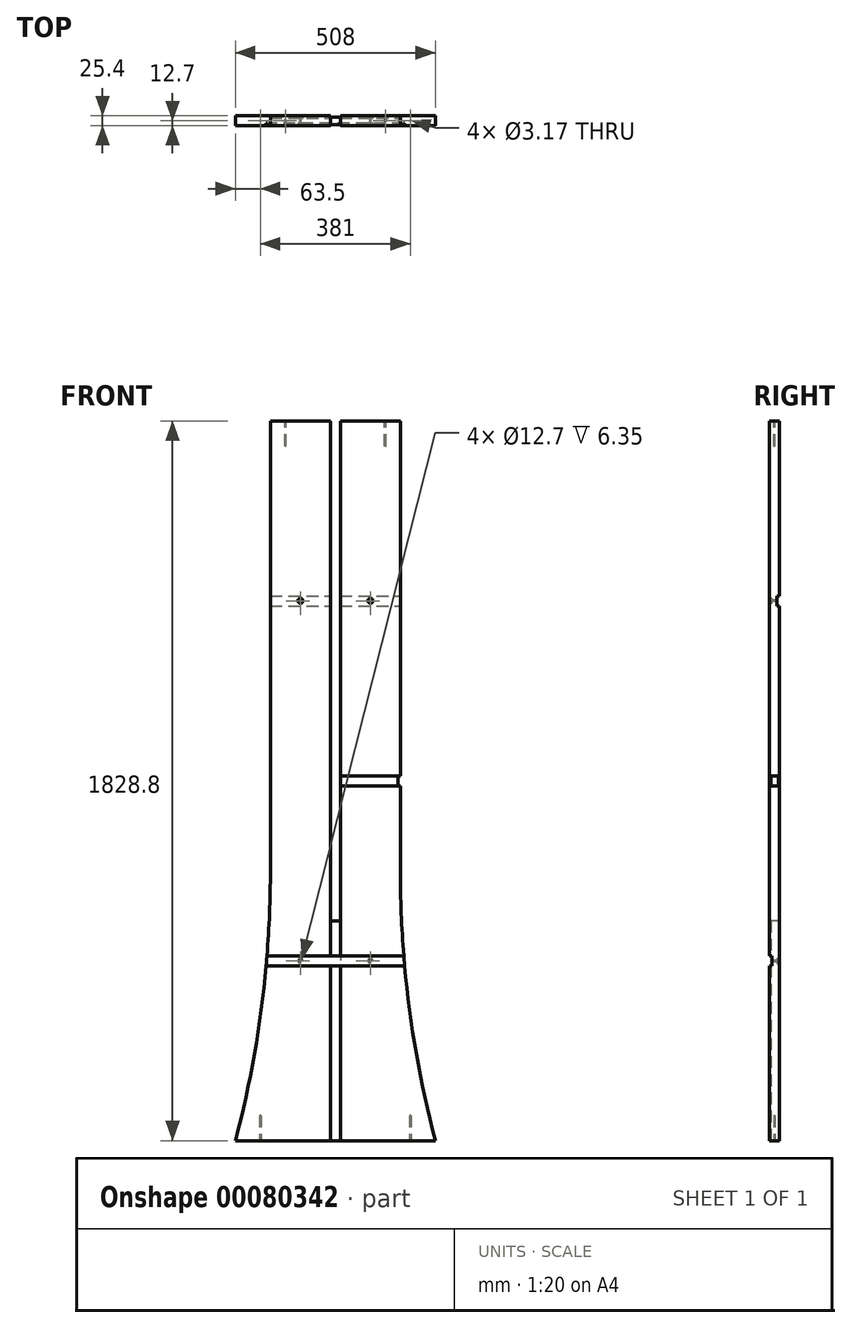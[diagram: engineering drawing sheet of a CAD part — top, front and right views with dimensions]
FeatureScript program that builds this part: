
annotation { "Feature Type Name" : "Feature", "Feature Type Description" : "" }
export const myFeature = defineFeature(function(context is Context, id is Id, definition is map)
    precondition{}
    {
        {
            var Q0;
            Q0=qCreatedBy(makeId("Front.planeOp"),FACE);
            var sketch = newSketch(context, id + "F0", { "sketchPlane" : qUnion([Q0])});
            skLineSegment(sketch, "E0", {"start": v(0, 0) * mm, "end": v(0, 1828.8) * mm, "construction": true});
            skLineSegment(sketch, "E1", {"start": v(0, 1828.8) * mm, "end": v(-165.1, 1828.8) * mm});
            skLineSegment(sketch, "E2", {"start": v(0, 0) * mm, "end": v(-254, 0) * mm});
            skLineSegment(sketch, "E3", {"start": v(-165.1, 1828.8) * mm, "end": v(-165.1, 685.8) * mm});
            skArc(sketch, "E4", {"start": v(-254, 0) * mm, "mid": v(-187.42, 340.03) * mm, "end": v(-165.1, 685.8) * mm});
            skLineSegment(sketch, "E5.MirrorCS", {"start": v(0, 1828.8) * mm, "end": v(165.1, 1828.8) * mm});
            skLineSegment(sketch, "E6.MirrorCS", {"start": v(165.1, 1828.8) * mm, "end": v(165.1, 685.8) * mm});
            skArc(sketch, "E7.MirrorCS", {"start": v(254, 0) * mm, "mid": v(187.42, 340.03) * mm, "end": v(165.1, 685.8) * mm});
            skLineSegment(sketch, "E8.MirrorCS", {"start": v(0, 0) * mm, "end": v(254, 0) * mm});
            skSolve(sketch);
        }
        {
            var Q0;
            Q0=makeQuery(id+"F0.imprint","IMPRINT",FACE,{"disambiguationData":[TD([[makeQuery(id+"F0.imprint","IMPRINT",EDGE,{"derivedFrom":sQuery(id+"F0.wireOp",EDGE,"E1")}),1.0]])]});
            extrude(context, id + "F1", {"entities" : qUnion([Q0]), "endBound" : BoundingType.SYMMETRIC, "depth" : 25.4 * mm});
        }
        {
            var Q0;
            Q0=makeQuery(id+"F1.opExtrude","CAP_FACE",FACE,{"disambiguationData":[OSD([sQuery(id+"F0.wireOp",EDGE,"E1"),sQuery(id+"F0.wireOp",EDGE,"E2"),sQuery(id+"F0.wireOp",EDGE,"E3"),sQuery(id+"F0.wireOp",EDGE,"E4"),sQuery(id+"F0.wireOp",EDGE,"E6.MirrorCS"),sQuery(id+"F0.wireOp",EDGE,"E5.MirrorCS"),sQuery(id+"F0.wireOp",EDGE,"E7.MirrorCS"),sQuery(id+"F0.wireOp",EDGE,"E8.MirrorCS")])],"isStart":false});
            var sketch = newSketch(context, id + "F24", { "sketchPlane" : qUnion([Q0])});
            skLineSegment(sketch, "E9", {"start": v(0, 1828.8) * mm, "end": v(0, 1828.8) * mm});
            skLineSegment(sketch, "E10", {"start": v(0, 1828.8) * mm, "end": v(0, 558.8) * mm, "construction": true});
            skLineSegment(sketch, "E11", {"start": v(0, 558.8) * mm, "end": v(12.7, 558.8) * mm});
            skLineSegment(sketch, "E12", {"start": v(12.7, 1828.8) * mm, "end": v(12.7, 558.8) * mm});
            skLineSegment(sketch, "E13", {"start": v(12.7, 1828.8) * mm, "end": v(0, 1828.8) * mm});
            skLineSegment(sketch, "E14.MirrorCS", {"start": v(-12.7, 1828.8) * mm, "end": v(-12.7, 558.8) * mm});
            skLineSegment(sketch, "E15.MirrorCS", {"start": v(0, 558.8) * mm, "end": v(-12.7, 558.8) * mm});
            skLineSegment(sketch, "E16.MirrorCS", {"start": v(-12.7, 1828.8) * mm, "end": v(0, 1828.8) * mm});
            skSolve(sketch);
        }
        {
            var Q0;
            Q0 = qSketchRegion(id + "F24", true);
            extrude(context, id + "F25", {"entities" : qUnion([Q0]), "operationType" : NewBodyOperationType.REMOVE, "oppositeDirection" : true, "depth" : 38.1 * mm});
        }
        {
            var Q0;
            Q0=makeQuery(id+"F1.opExtrude","CAP_FACE",FACE,{"disambiguationData":[OSD([sQuery(id+"F0.wireOp",EDGE,"E1"),sQuery(id+"F0.wireOp",EDGE,"E2"),sQuery(id+"F0.wireOp",EDGE,"E3"),sQuery(id+"F0.wireOp",EDGE,"E4"),sQuery(id+"F0.wireOp",EDGE,"E6.MirrorCS"),sQuery(id+"F0.wireOp",EDGE,"E5.MirrorCS"),sQuery(id+"F0.wireOp",EDGE,"E7.MirrorCS"),sQuery(id+"F0.wireOp",EDGE,"E8.MirrorCS")])],"isStart":false});
            var sketch = newSketch(context, id + "F2", { "sketchPlane" : qUnion([Q0])});
            skPoint(sketch, "E17", {"position": v(-88.9, 1371.6) * mm});
            skPoint(sketch, "E18", {"position": v(88.9, 1371.6) * mm});
            skSolve(sketch);
        }
        {
            var Q0;
            Q0=sQuery(id+"F2.wireOp",VERTEX,"E17");
            var Q1;
            Q1=sQuery(id+"F2.wireOp",VERTEX,"E18");
            var Q2;
            Q2=makeQuery(id+"F1.opExtrude","SWEPT_BODY",BODY,{"disambiguationData":[OSD([sQuery(id+"F0.wireOp",EDGE,"E1"),sQuery(id+"F0.wireOp",EDGE,"E2"),sQuery(id+"F0.wireOp",EDGE,"E3"),sQuery(id+"F0.wireOp",EDGE,"E4"),sQuery(id+"F0.wireOp",EDGE,"E6.MirrorCS"),sQuery(id+"F0.wireOp",EDGE,"E5.MirrorCS"),sQuery(id+"F0.wireOp",EDGE,"E7.MirrorCS"),sQuery(id+"F0.wireOp",EDGE,"E8.MirrorCS")])]});
            hole(context, id + "F3", {"style" : HoleStyle.C_BORE, "endStyle" : HoleEndStyle.BLIND, "holeDiameter" : 3.17 * mm, "cBoreDiameter" : 12.7 * mm, "cBoreDepth" : 6.35 * mm, "holeDepth" : 63.5 * mm, "locations" : qUnion([Q0, Q1]), "scope" : qUnion([Q2])});
        }
        {
            var Q0;
            Q0=makeQuery(id+"F1.opExtrude","CAP_FACE",FACE,{"disambiguationData":[OSD([sQuery(id+"F0.wireOp",EDGE,"E1"),sQuery(id+"F0.wireOp",EDGE,"E2"),sQuery(id+"F0.wireOp",EDGE,"E3"),sQuery(id+"F0.wireOp",EDGE,"E4"),sQuery(id+"F0.wireOp",EDGE,"E6.MirrorCS"),sQuery(id+"F0.wireOp",EDGE,"E5.MirrorCS"),sQuery(id+"F0.wireOp",EDGE,"E7.MirrorCS"),sQuery(id+"F0.wireOp",EDGE,"E8.MirrorCS")])],"isStart":true});
            var sketch = newSketch(context, id + "F4", { "sketchPlane" : qUnion([Q0])});
            skPoint(sketch, "E19", {"position": v(-88.9, 457.2) * mm});
            skPoint(sketch, "E20", {"position": v(88.9, 457.2) * mm});
            skSolve(sketch);
        }
        {
            var Q0;
            Q0=sQuery(id+"F4.wireOp",VERTEX,"E19");
            var Q1;
            Q1=sQuery(id+"F4.wireOp",VERTEX,"E20");
            var Q2;
            Q2=makeQuery(id+"F1.opExtrude","SWEPT_BODY",BODY,{"disambiguationData":[OSD([sQuery(id+"F0.wireOp",EDGE,"E1"),sQuery(id+"F0.wireOp",EDGE,"E2"),sQuery(id+"F0.wireOp",EDGE,"E3"),sQuery(id+"F0.wireOp",EDGE,"E4"),sQuery(id+"F0.wireOp",EDGE,"E6.MirrorCS"),sQuery(id+"F0.wireOp",EDGE,"E5.MirrorCS"),sQuery(id+"F0.wireOp",EDGE,"E7.MirrorCS"),sQuery(id+"F0.wireOp",EDGE,"E8.MirrorCS")])]});
            hole(context, id + "F5", {"style" : HoleStyle.C_BORE, "endStyle" : HoleEndStyle.BLIND, "holeDiameter" : 3.17 * mm, "cBoreDiameter" : 12.7 * mm, "cBoreDepth" : 6.35 * mm, "holeDepth" : 63.5 * mm, "locations" : qUnion([Q0, Q1]), "scope" : qUnion([Q2])});
        }
        {
            var Q0;
            {var subQ2=sQuery(id+"F0.wireOp",EDGE,"E5.MirrorCS");var subQ5=sQuery(id+"F0.wireOp",EDGE,"E3");var subQ7=sQuery(id+"F0.wireOp",EDGE,"E1");Q0=makeQuery(id+"F25.boolean.opBoolean","SPLIT",FACE,{"disambiguationData":[TD([makeQuery(id+"F1.opExtrude","SWEPT_FACE",FACE,{"disambiguationData":[OSD([subQ5])]})])],"derivedFrom":makeQuery(id+"F1.opExtrude","SWEPT_FACE",FACE,{"disambiguationData":[OSD([subQ7,subQ2])]})});}
            var sketch = newSketch(context, id + "F6", { "sketchPlane" : qUnion([Q0])});
            skPoint(sketch, "E21", {"position": v(-127, 0) * mm});
            skPoint(sketch, "E22", {"position": v(127, 0) * mm});
            skSolve(sketch);
        }
        {
            var Q0;
            Q0=sQuery(id+"F6.wireOp",VERTEX,"E21");
            var Q1;
            Q1=sQuery(id+"F6.wireOp",VERTEX,"E22");
            var Q2;
            Q2=makeQuery(id+"F1.opExtrude","SWEPT_BODY",BODY,{"disambiguationData":[OSD([sQuery(id+"F0.wireOp",EDGE,"E1"),sQuery(id+"F0.wireOp",EDGE,"E2"),sQuery(id+"F0.wireOp",EDGE,"E3"),sQuery(id+"F0.wireOp",EDGE,"E4"),sQuery(id+"F0.wireOp",EDGE,"E6.MirrorCS"),sQuery(id+"F0.wireOp",EDGE,"E5.MirrorCS"),sQuery(id+"F0.wireOp",EDGE,"E7.MirrorCS"),sQuery(id+"F0.wireOp",EDGE,"E8.MirrorCS")])]});
            hole(context, id + "F7", {"style" : HoleStyle.SIMPLE, "endStyle" : HoleEndStyle.BLIND, "holeDiameter" : 3.17 * mm, "holeDepth" : 63.5 * mm, "locations" : qUnion([Q0, Q1]), "scope" : qUnion([Q2])});
        }
        {
            var Q0;
            Q0=makeQuery(id+"F1.opExtrude","SWEPT_FACE",FACE,{"disambiguationData":[OSD([sQuery(id+"F0.wireOp",EDGE,"E2"),sQuery(id+"F0.wireOp",EDGE,"E8.MirrorCS")])]});
            var sketch = newSketch(context, id + "F8", { "sketchPlane" : qUnion([Q0])});
            skPoint(sketch, "E23", {"position": v(-190.5, 0) * mm});
            skPoint(sketch, "E24", {"position": v(190.5, 0) * mm});
            skSolve(sketch);
        }
        {
            var Q0;
            Q0=sQuery(id+"F8.wireOp",VERTEX,"E23");
            var Q1;
            Q1=sQuery(id+"F8.wireOp",VERTEX,"E24");
            var Q2;
            Q2=makeQuery(id+"F1.opExtrude","SWEPT_BODY",BODY,{"disambiguationData":[OSD([sQuery(id+"F0.wireOp",EDGE,"E1"),sQuery(id+"F0.wireOp",EDGE,"E2"),sQuery(id+"F0.wireOp",EDGE,"E3"),sQuery(id+"F0.wireOp",EDGE,"E4"),sQuery(id+"F0.wireOp",EDGE,"E6.MirrorCS"),sQuery(id+"F0.wireOp",EDGE,"E5.MirrorCS"),sQuery(id+"F0.wireOp",EDGE,"E7.MirrorCS"),sQuery(id+"F0.wireOp",EDGE,"E8.MirrorCS")])]});
            hole(context, id + "F9", {"style" : HoleStyle.SIMPLE, "endStyle" : HoleEndStyle.BLIND, "holeDiameter" : 3.17 * mm, "holeDepth" : 63.5 * mm, "locations" : qUnion([Q0, Q1]), "scope" : qUnion([Q2])});
        }
        {
            var Q0;
            Q0=makeQuery(id+"F1.opExtrude","CAP_FACE",FACE,{"disambiguationData":[OSD([sQuery(id+"F0.wireOp",EDGE,"E1"),sQuery(id+"F0.wireOp",EDGE,"E2"),sQuery(id+"F0.wireOp",EDGE,"E3"),sQuery(id+"F0.wireOp",EDGE,"E4"),sQuery(id+"F0.wireOp",EDGE,"E6.MirrorCS"),sQuery(id+"F0.wireOp",EDGE,"E5.MirrorCS"),sQuery(id+"F0.wireOp",EDGE,"E7.MirrorCS"),sQuery(id+"F0.wireOp",EDGE,"E8.MirrorCS")])],"isStart":true});
            var sketch = newSketch(context, id + "F10", { "sketchPlane" : qUnion([Q0])});
            skLineSegment(sketch, "E25", {"start": v(-88.9, 1371.6) * mm, "end": v(88.9, 1371.6) * mm, "construction": true});
            skLineSegment(sketch, "E26", {"start": v(88.9, 1371.6) * mm, "end": v(165.1, 1371.6) * mm, "construction": true});
            skLineSegment(sketch, "E27", {"start": v(-88.9, 1371.6) * mm, "end": v(-165.1, 1371.6) * mm, "construction": true});
            skLineSegment(sketch, "E28.bottom", {"start": v(165.1, 1384.3) * mm, "end": v(-165.1, 1384.3) * mm});
            skLineSegment(sketch, "E28.top", {"start": v(165.1, 1358.9) * mm, "end": v(-165.1, 1358.9) * mm});
            skLineSegment(sketch, "E28.left", {"start": v(165.1, 1384.3) * mm, "end": v(165.1, 1358.9) * mm});
            skLineSegment(sketch, "E28.right", {"start": v(-165.1, 1384.3) * mm, "end": v(-165.1, 1358.9) * mm});
            skPoint(sketch, "E28.middle", {"position": v(0, 1371.6) * mm});
            skSolve(sketch);
        }
        {
            var Q0;
            Q0 = qSketchRegion(id + "F10", true);
            extrude(context, id + "F11", {"entities" : qUnion([Q0]), "operationType" : NewBodyOperationType.REMOVE, "oppositeDirection" : true, "depth" : 6.35 * mm});
        }
        {
            var Q0;
            Q0=makeQuery(id+"F1.opExtrude","CAP_FACE",FACE,{"disambiguationData":[OSD([sQuery(id+"F0.wireOp",EDGE,"E1"),sQuery(id+"F0.wireOp",EDGE,"E2"),sQuery(id+"F0.wireOp",EDGE,"E3"),sQuery(id+"F0.wireOp",EDGE,"E4"),sQuery(id+"F0.wireOp",EDGE,"E6.MirrorCS"),sQuery(id+"F0.wireOp",EDGE,"E5.MirrorCS"),sQuery(id+"F0.wireOp",EDGE,"E7.MirrorCS"),sQuery(id+"F0.wireOp",EDGE,"E8.MirrorCS")])],"isStart":false});
            var sketch = newSketch(context, id + "F12", { "sketchPlane" : qUnion([Q0])});
            skLineSegment(sketch, "E29", {"start": v(-88.9, 457.2) * mm, "end": v(88.9, 457.2) * mm, "construction": true});
            skLineSegment(sketch, "E30", {"start": v(88.9, 457.2) * mm, "end": v(226.48, 457.2) * mm, "construction": true});
            skLineSegment(sketch, "E31", {"start": v(-88.9, 457.2) * mm, "end": v(-250.88, 457.2) * mm, "construction": true});
            skLineSegment(sketch, "E32.bottom", {"start": v(213.47, 444.5) * mm, "end": v(-213.47, 444.5) * mm});
            skLineSegment(sketch, "E32.top", {"start": v(213.47, 469.9) * mm, "end": v(-213.47, 469.9) * mm});
            skLineSegment(sketch, "E32.left", {"start": v(213.47, 444.5) * mm, "end": v(213.47, 469.9) * mm});
            skLineSegment(sketch, "E32.right", {"start": v(-213.47, 444.5) * mm, "end": v(-213.47, 469.9) * mm});
            skPoint(sketch, "E32.middle", {"position": v(0, 457.2) * mm});
            skSolve(sketch);
        }
        {
            var Q0;
            Q0 = qSketchRegion(id + "F12", true);
            extrude(context, id + "F13", {"entities" : qUnion([Q0]), "operationType" : NewBodyOperationType.REMOVE, "oppositeDirection" : true, "depth" : 6.35 * mm});
        }
        {
            var Q0;
            {var subQ0=sQuery(id+"F0.wireOp",EDGE,"E7.MirrorCS");var subQ1=sQuery(id+"F0.wireOp",EDGE,"E8.MirrorCS");var subQ2=sQuery(id+"F0.wireOp",EDGE,"E2");var subQ3=sQuery(id+"F0.wireOp",EDGE,"E3");var subQ4=sQuery(id+"F0.wireOp",EDGE,"E4");var subQ5=sQuery(id+"F0.wireOp",EDGE,"E6.MirrorCS");Q0=makeQuery(id+"F11.boolean.opBoolean","SPLIT",FACE,{"disambiguationData":[TD([makeQuery(id+"F1.opExtrude","SWEPT_FACE",FACE,{"disambiguationData":[OSD([subQ2,subQ1])]}),makeQuery(id+"F1.opExtrude","SWEPT_FACE",FACE,{"disambiguationData":[OSD([subQ3])]}),makeQuery(id+"F1.opExtrude","SWEPT_FACE",FACE,{"disambiguationData":[OSD([subQ4])]}),makeQuery(id+"F1.opExtrude","SWEPT_FACE",FACE,{"disambiguationData":[OSD([subQ5])]}),makeQuery(id+"F1.opExtrude","SWEPT_FACE",FACE,{"disambiguationData":[OSD([subQ0])]}),makeQuery(id+"F25.boolean.opBoolean","COPY",FACE,{"derivedFrom":makeQuery(id+"F25.opExtrude","SWEPT_FACE",FACE,{"disambiguationData":[OSD([sQuery(id+"F24.wireOp",EDGE,"E11"),sQuery(id+"F24.wireOp",EDGE,"E15.MirrorCS")])]})}),makeQuery(id+"F25.boolean.opBoolean","COPY",FACE,{"derivedFrom":makeQuery(id+"F25.opExtrude","SWEPT_FACE",FACE,{"disambiguationData":[OSD([sQuery(id+"F24.wireOp",EDGE,"E12")])]})}),makeQuery(id+"F25.boolean.opBoolean","COPY",FACE,{"derivedFrom":makeQuery(id+"F25.opExtrude","SWEPT_FACE",FACE,{"disambiguationData":[OSD([sQuery(id+"F24.wireOp",EDGE,"E14.MirrorCS")])]})}),makeQuery(id+"F5.hole-0.boolean.opBoolean","COPY",FACE,{"derivedFrom":makeQuery(id+"F5.hole-0.opRevolve","SWEPT_FACE",FACE,{"disambiguationData":[OSD([sQuery(id+"F5.hole-0.sketch.wireOp",EDGE,"cbore_start_line_2")])]})}),makeQuery(id+"F5.hole-1.boolean.opBoolean","COPY",FACE,{"derivedFrom":makeQuery(id+"F5.hole-1.opRevolve","SWEPT_FACE",FACE,{"disambiguationData":[OSD([sQuery(id+"F5.hole-1.sketch.wireOp",EDGE,"cbore_start_line_2")])]})}),makeQuery(id+"F11.opExtrude","SWEPT_FACE",FACE,{"disambiguationData":[OSD([sQuery(id+"F10.wireOp",EDGE,"E28.top")])]})])],"derivedFrom":makeQuery(id+"F1.opExtrude","CAP_FACE",FACE,{"disambiguationData":[OSD([sQuery(id+"F0.wireOp",EDGE,"E1"),subQ2,subQ3,subQ4,subQ5,sQuery(id+"F0.wireOp",EDGE,"E5.MirrorCS"),subQ0,subQ1])],"isStart":true})});}
            var sketch = newSketch(context, id + "F14", { "sketchPlane" : qUnion([Q0])});
            skLineSegment(sketch, "E33.bottom", {"start": v(-12.7, 558.8) * mm, "end": v(12.7, 558.8) * mm});
            skLineSegment(sketch, "E33.top", {"start": v(-12.7, 0) * mm, "end": v(12.7, 0) * mm});
            skLineSegment(sketch, "E33.left", {"start": v(-12.7, 558.8) * mm, "end": v(-12.7, 0) * mm});
            skLineSegment(sketch, "E33.right", {"start": v(12.7, 558.8) * mm, "end": v(12.7, 0) * mm});
            skSolve(sketch);
        }
        {
            var Q0;
            Q0 = qSketchRegion(id + "F14", true);
            extrude(context, id + "F15", {"entities" : qUnion([Q0]), "operationType" : NewBodyOperationType.REMOVE, "oppositeDirection" : true, "depth" : 3.17 * mm});
        }
        {
            var Q0;
            {var subQ0=sQuery(id+"F0.wireOp",EDGE,"E5.MirrorCS");var subQ1=sQuery(id+"F0.wireOp",EDGE,"E1");var subQ2=sQuery(id+"F0.wireOp",EDGE,"E7.MirrorCS");var subQ3=sQuery(id+"F0.wireOp",EDGE,"E3");var subQ4=sQuery(id+"F0.wireOp",EDGE,"E4");var subQ5=sQuery(id+"F0.wireOp",EDGE,"E6.MirrorCS");Q0=makeQuery(id+"F13.boolean.opBoolean","SPLIT",FACE,{"disambiguationData":[TD([makeQuery(id+"F1.opExtrude","SWEPT_FACE",FACE,{"disambiguationData":[OSD([subQ3])]})])],"derivedFrom":makeQuery(id+"F1.opExtrude","CAP_FACE",FACE,{"disambiguationData":[OSD([subQ1,sQuery(id+"F0.wireOp",EDGE,"E2"),subQ3,subQ4,subQ5,subQ0,subQ2,sQuery(id+"F0.wireOp",EDGE,"E8.MirrorCS")])],"isStart":false})});}
            var sketch = newSketch(context, id + "F16", { "sketchPlane" : qUnion([Q0])});
            skLineSegment(sketch, "E34.bottom", {"start": v(-12.7, 558.8) * mm, "end": v(12.7, 558.8) * mm});
            skLineSegment(sketch, "E34.top", {"start": v(-12.7, 0) * mm, "end": v(12.7, 0) * mm});
            skLineSegment(sketch, "E34.left", {"start": v(-12.7, 558.8) * mm, "end": v(-12.7, 0) * mm});
            skLineSegment(sketch, "E34.right", {"start": v(12.7, 558.8) * mm, "end": v(12.7, 0) * mm});
            skSolve(sketch);
        }
        {
            var Q0;
            Q0 = qSketchRegion(id + "F16", true);
            extrude(context, id + "F17", {"entities" : qUnion([Q0]), "operationType" : NewBodyOperationType.REMOVE, "oppositeDirection" : true, "depth" : 3.17 * mm});
        }
        {
            var Q0;
            {var subQ1=sQuery(id+"F0.wireOp",EDGE,"E5.MirrorCS");var subQ2=sQuery(id+"F0.wireOp",EDGE,"E1");var subQ4=sQuery(id+"F0.wireOp",EDGE,"E7.MirrorCS");var subQ7=sQuery(id+"F0.wireOp",EDGE,"E6.MirrorCS");var subQ8=makeQuery(id+"F1.opExtrude","SWEPT_FACE",FACE,{"disambiguationData":[OSD([subQ7])]});var subQ10=sQuery(id+"F0.wireOp",EDGE,"E3");var subQ11=sQuery(id+"F0.wireOp",EDGE,"E4");Q0=makeQuery(id+"F17.boolean.opBoolean","SPLIT",FACE,{"disambiguationData":[TD([subQ8])],"derivedFrom":makeQuery(id+"F13.boolean.opBoolean","SPLIT",FACE,{"disambiguationData":[TD([makeQuery(id+"F1.opExtrude","SWEPT_FACE",FACE,{"disambiguationData":[OSD([subQ10])]})])],"derivedFrom":makeQuery(id+"F1.opExtrude","CAP_FACE",FACE,{"disambiguationData":[OSD([subQ2,sQuery(id+"F0.wireOp",EDGE,"E2"),subQ10,subQ11,subQ7,subQ1,subQ4,sQuery(id+"F0.wireOp",EDGE,"E8.MirrorCS")])],"isStart":false})})});}
            var sketch = newSketch(context, id + "F18", { "sketchPlane" : qUnion([Q0])});
            skLineSegment(sketch, "E35", {"start": v(0, 0) * mm, "end": v(0, 914.4) * mm, "construction": true});
            skLineSegment(sketch, "E36", {"start": v(0, 914.4) * mm, "end": v(0, 927.1) * mm, "construction": true});
            skLineSegment(sketch, "E37", {"start": v(0, 914.4) * mm, "end": v(165.1, 914.4) * mm, "construction": true});
            skLineSegment(sketch, "E38.bottom", {"start": v(0, 927.1) * mm, "end": v(165.1, 927.1) * mm});
            skLineSegment(sketch, "E38.top", {"start": v(0, 901.7) * mm, "end": v(165.1, 901.7) * mm});
            skLineSegment(sketch, "E38.left", {"start": v(0, 927.1) * mm, "end": v(0, 901.7) * mm});
            skLineSegment(sketch, "E38.right", {"start": v(165.1, 927.1) * mm, "end": v(165.1, 901.7) * mm});
            skPoint(sketch, "E38.middle", {"position": v(82.55, 914.4) * mm});
            skSolve(sketch);
        }
        {
            var Q0;
            {var subQ1=sQuery(id+"F0.wireOp",EDGE,"E5.MirrorCS");var subQ2=sQuery(id+"F0.wireOp",EDGE,"E1");var subQ4=sQuery(id+"F0.wireOp",EDGE,"E7.MirrorCS");var subQ7=sQuery(id+"F0.wireOp",EDGE,"E6.MirrorCS");var subQ8=makeQuery(id+"F1.opExtrude","SWEPT_FACE",FACE,{"disambiguationData":[OSD([subQ7])]});var subQ10=sQuery(id+"F0.wireOp",EDGE,"E3");var subQ11=sQuery(id+"F0.wireOp",EDGE,"E4");Q0=makeQuery(id+"F17.boolean.opBoolean","SPLIT",FACE,{"disambiguationData":[TD([subQ8])],"derivedFrom":makeQuery(id+"F13.boolean.opBoolean","SPLIT",FACE,{"disambiguationData":[TD([makeQuery(id+"F1.opExtrude","SWEPT_FACE",FACE,{"disambiguationData":[OSD([subQ10])]})])],"derivedFrom":makeQuery(id+"F1.opExtrude","CAP_FACE",FACE,{"disambiguationData":[OSD([subQ2,sQuery(id+"F0.wireOp",EDGE,"E2"),subQ10,subQ11,subQ7,subQ1,subQ4,sQuery(id+"F0.wireOp",EDGE,"E8.MirrorCS")])],"isStart":false})})});}
            var sketch = newSketch(context, id + "F19", { "sketchPlane" : qUnion([Q0])});
            skLineSegment(sketch, "E39", {"start": v(0, 0) * mm, "end": v(0, 914.4) * mm, "construction": true});
            skLineSegment(sketch, "E40", {"start": v(0, 914.4) * mm, "end": v(165.1, 914.4) * mm, "construction": true});
            skLineSegment(sketch, "E41.bottom", {"start": v(158.75, 901.7) * mm, "end": v(171.45, 901.7) * mm});
            skLineSegment(sketch, "E41.top", {"start": v(158.75, 927.1) * mm, "end": v(171.45, 927.1) * mm});
            skLineSegment(sketch, "E41.left", {"start": v(158.75, 901.7) * mm, "end": v(158.75, 927.1) * mm});
            skLineSegment(sketch, "E41.right", {"start": v(171.45, 901.7) * mm, "end": v(171.45, 927.1) * mm});
            skPoint(sketch, "E41.middle", {"position": v(165.1, 914.4) * mm});
            skSolve(sketch);
        }
        {
            var Q0;
            Q0 = qSketchRegion(id + "F19", true);
            extrude(context, id + "F20", {"entities" : qUnion([Q0]), "operationType" : NewBodyOperationType.REMOVE, "oppositeDirection" : true, "depth" : 25.4 * mm});
        }
        {
            var Q0;
            Q0 = qSketchRegion(id + "F18", true);
            extrude(context, id + "F21", {"entities" : qUnion([Q0]), "operationType" : NewBodyOperationType.REMOVE, "oppositeDirection" : true, "depth" : 3.17 * mm});
        }
        {
            var Q0;
            {var subQ0=makeQuery(id+"F25.boolean.opBoolean","COPY",FACE,{"derivedFrom":makeQuery(id+"F25.opExtrude","SWEPT_FACE",FACE,{"disambiguationData":[OSD([sQuery(id+"F24.wireOp",EDGE,"E12")])]})});var subQ1=sQuery(id+"F0.wireOp",EDGE,"E7.MirrorCS");var subQ2=makeQuery(id+"F1.opExtrude","SWEPT_FACE",FACE,{"disambiguationData":[OSD([subQ1])]});var subQ3=sQuery(id+"F0.wireOp",EDGE,"E6.MirrorCS");var subQ4=makeQuery(id+"F1.opExtrude","SWEPT_FACE",FACE,{"disambiguationData":[OSD([subQ3])]});var subQ5=makeQuery(id+"F5.hole-0.boolean.opBoolean","COPY",FACE,{"derivedFrom":makeQuery(id+"F5.hole-0.opRevolve","SWEPT_FACE",FACE,{"disambiguationData":[OSD([sQuery(id+"F5.hole-0.sketch.wireOp",EDGE,"cbore_start_line_2")])]})});var subQ6=sQuery(id+"F0.wireOp",EDGE,"E8.MirrorCS");var subQ7=sQuery(id+"F0.wireOp",EDGE,"E2");var subQ8=makeQuery(id+"F1.opExtrude","SWEPT_FACE",FACE,{"disambiguationData":[OSD([subQ7,subQ6])]});var subQ9=makeQuery(id+"F11.opExtrude","SWEPT_FACE",FACE,{"disambiguationData":[OSD([sQuery(id+"F10.wireOp",EDGE,"E28.top")])]});var subQ10=sQuery(id+"F0.wireOp",EDGE,"E3");var subQ11=sQuery(id+"F0.wireOp",EDGE,"E4");Q0=makeQuery(id+"F15.boolean.opBoolean","SPLIT",FACE,{"disambiguationData":[TD([subQ4])],"derivedFrom":makeQuery(id+"F11.boolean.opBoolean","SPLIT",FACE,{"disambiguationData":[TD([subQ8,makeQuery(id+"F1.opExtrude","SWEPT_FACE",FACE,{"disambiguationData":[OSD([subQ10])]}),makeQuery(id+"F1.opExtrude","SWEPT_FACE",FACE,{"disambiguationData":[OSD([subQ11])]}),subQ4,subQ2,makeQuery(id+"F25.boolean.opBoolean","COPY",FACE,{"derivedFrom":makeQuery(id+"F25.opExtrude","SWEPT_FACE",FACE,{"disambiguationData":[OSD([sQuery(id+"F24.wireOp",EDGE,"E11"),sQuery(id+"F24.wireOp",EDGE,"E15.MirrorCS")])]})}),subQ0,makeQuery(id+"F25.boolean.opBoolean","COPY",FACE,{"derivedFrom":makeQuery(id+"F25.opExtrude","SWEPT_FACE",FACE,{"disambiguationData":[OSD([sQuery(id+"F24.wireOp",EDGE,"E14.MirrorCS")])]})}),subQ5,makeQuery(id+"F5.hole-1.boolean.opBoolean","COPY",FACE,{"derivedFrom":makeQuery(id+"F5.hole-1.opRevolve","SWEPT_FACE",FACE,{"disambiguationData":[OSD([sQuery(id+"F5.hole-1.sketch.wireOp",EDGE,"cbore_start_line_2")])]})}),subQ9])],"derivedFrom":makeQuery(id+"F1.opExtrude","CAP_FACE",FACE,{"disambiguationData":[OSD([sQuery(id+"F0.wireOp",EDGE,"E1"),subQ7,subQ10,subQ11,subQ3,sQuery(id+"F0.wireOp",EDGE,"E5.MirrorCS"),subQ1,subQ6])],"isStart":true})})});}
            var sketch = newSketch(context, id + "F22", { "sketchPlane" : qUnion([Q0])});
            skLineSegment(sketch, "E42", {"start": v(0, 0) * mm, "end": v(0, 914.4) * mm, "construction": true});
            skLineSegment(sketch, "E43", {"start": v(0, 914.4) * mm, "end": v(0, 927.1) * mm, "construction": true});
            skLineSegment(sketch, "E44", {"start": v(0, 914.4) * mm, "end": v(-165.1, 914.4) * mm, "construction": true});
            skLineSegment(sketch, "E45.bottom", {"start": v(0, 927.1) * mm, "end": v(-165.1, 927.1) * mm});
            skLineSegment(sketch, "E45.top", {"start": v(0, 901.7) * mm, "end": v(-165.1, 901.7) * mm});
            skLineSegment(sketch, "E45.left", {"start": v(0, 927.1) * mm, "end": v(0, 901.7) * mm});
            skLineSegment(sketch, "E45.right", {"start": v(-165.1, 927.1) * mm, "end": v(-165.1, 901.7) * mm});
            skPoint(sketch, "E45.middle", {"position": v(-82.55, 914.4) * mm});
            skSolve(sketch);
        }
        {
            var Q0;
            Q0 = qSketchRegion(id + "F22", true);
            extrude(context, id + "F23", {"entities" : qUnion([Q0]), "operationType" : NewBodyOperationType.REMOVE, "oppositeDirection" : true, "depth" : 3.17 * mm});
        }
    });
